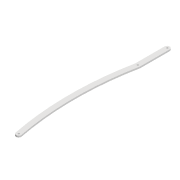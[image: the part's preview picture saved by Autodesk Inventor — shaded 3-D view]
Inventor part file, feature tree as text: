
AUTODESK INVENTOR PART (.ipt)
format: ipt  version: 2022 (Build 260153000, 153)  size: 99,840 bytes
history: native  units: mm
features: extrude x1, sketch x1
ambient origin geometry x8: Origin, YZ Plane, XZ Plane, XY Plane, X Axis, Y Axis, Z Axis, Center Point
bodies: Solid1 (feature_tree)
feature tree (2):
  extrude  "Extrusion1"  Depth=600.0mm
  sketch  "Sketch1"  dims[d0=3.3mm d1=3.3mm d2=10.0mm d3=288.984mm d6=3.0mm d7=0.0mm d14=3.3mm d15=231.585mm d18=600.0mm d19=600.0mm]
